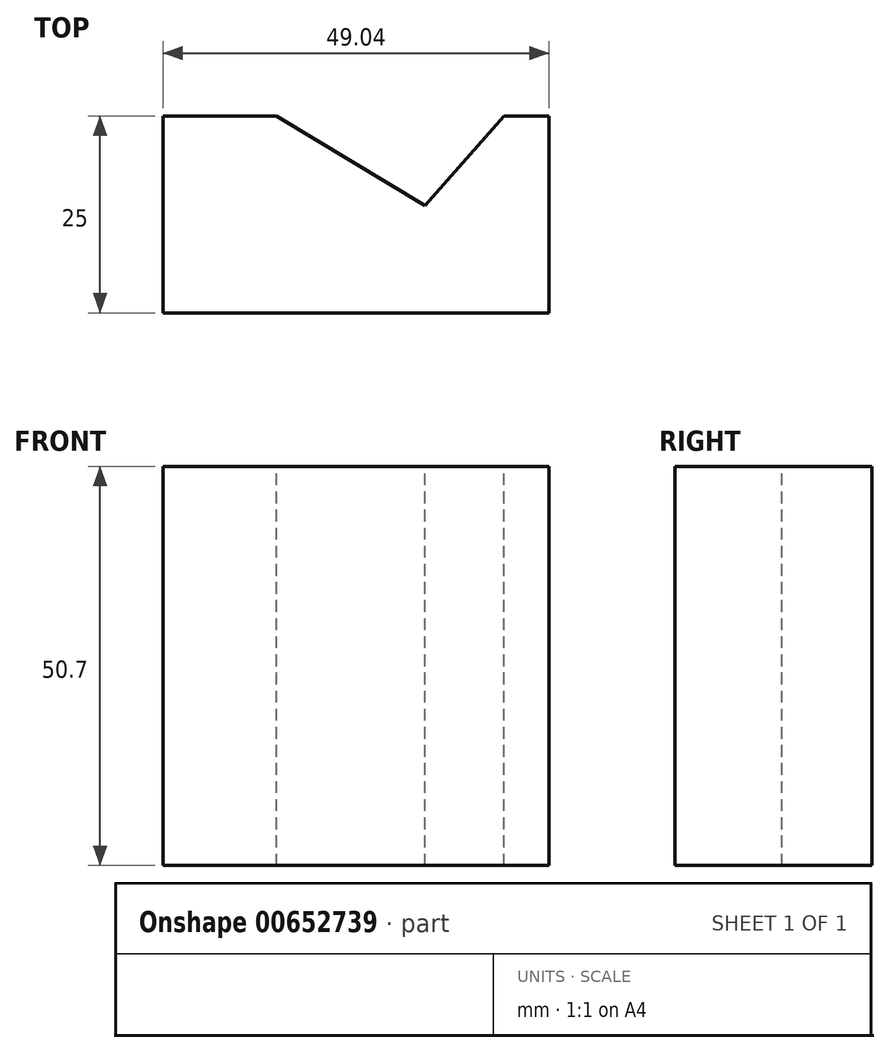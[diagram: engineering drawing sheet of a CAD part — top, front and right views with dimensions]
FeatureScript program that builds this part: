
annotation { "Feature Type Name" : "Feature", "Feature Type Description" : "" }
export const myFeature = defineFeature(function(context is Context, id is Id, definition is map)
    precondition{}
    {
        {
            var Q0;
            Q0=qCreatedBy(makeId("Front.planeOp"),FACE);
            var sketch = newSketch(context, id + "F0", { "sketchPlane" : qUnion([Q0])});
            skLineSegment(sketch, "E0.bottom", {"start": v(-44.47, 24.94) * mm, "end": v(4.57, 24.94) * mm});
            skLineSegment(sketch, "E0.top", {"start": v(-44.47, -25.76) * mm, "end": v(4.57, -25.76) * mm});
            skLineSegment(sketch, "E0.left", {"start": v(-44.47, 24.94) * mm, "end": v(-44.47, -25.76) * mm});
            skLineSegment(sketch, "E0.right", {"start": v(4.57, 24.94) * mm, "end": v(4.57, -25.76) * mm});
            skSolve(sketch);
        }
        {
            var Q0;
            Q0=makeQuery(id+"F0.imprint","IMPRINT",FACE,{"disambiguationData":[TD([[makeQuery(id+"F0.imprint","IMPRINT",EDGE,{"derivedFrom":sQuery(id+"F0.wireOp",EDGE,"E0.bottom")}),-1.0]])]});
            extrude(context, id + "F1", {"entities" : qUnion([Q0]), "depth" : 25 * mm, "offsetDistance" : 25 * mm});
        }
        {
            var Q0;
            Q0=makeQuery(id+"F1.opExtrude","SWEPT_FACE",FACE,{"disambiguationData":[OSD([sQuery(id+"F0.wireOp",EDGE,"E0.bottom")])]});
            var sketch = newSketch(context, id + "F2", { "sketchPlane" : qUnion([Q0])});
            skLineSegment(sketch, "E1", {"start": v(-30.06, 0) * mm, "end": v(-11.19, -11.4) * mm});
            skLineSegment(sketch, "E2", {"start": v(-11.19, -11.4) * mm, "end": v(-1.17, 0) * mm});
            skSolve(sketch);
        }
        {
            var Q0;
            {var subQ0=sQuery(id+"F2.wireOp",EDGE,"E1");Q0=makeQuery(id+"F2.imprint","IMPRINT",FACE,{"disambiguationData":[TD([[makeQuery(id+"F2.imprint","IMPRINT",EDGE,{"derivedFrom":subQ0}),1.0]])]});}
            extrude(context, id + "F3", {"entities" : qUnion([Q0]), "operationType" : NewBodyOperationType.REMOVE, "endBound" : BoundingType.THROUGH_ALL, "oppositeDirection" : true, "depth" : 25 * mm, "offsetDistance" : 25 * mm});
        }
    });
